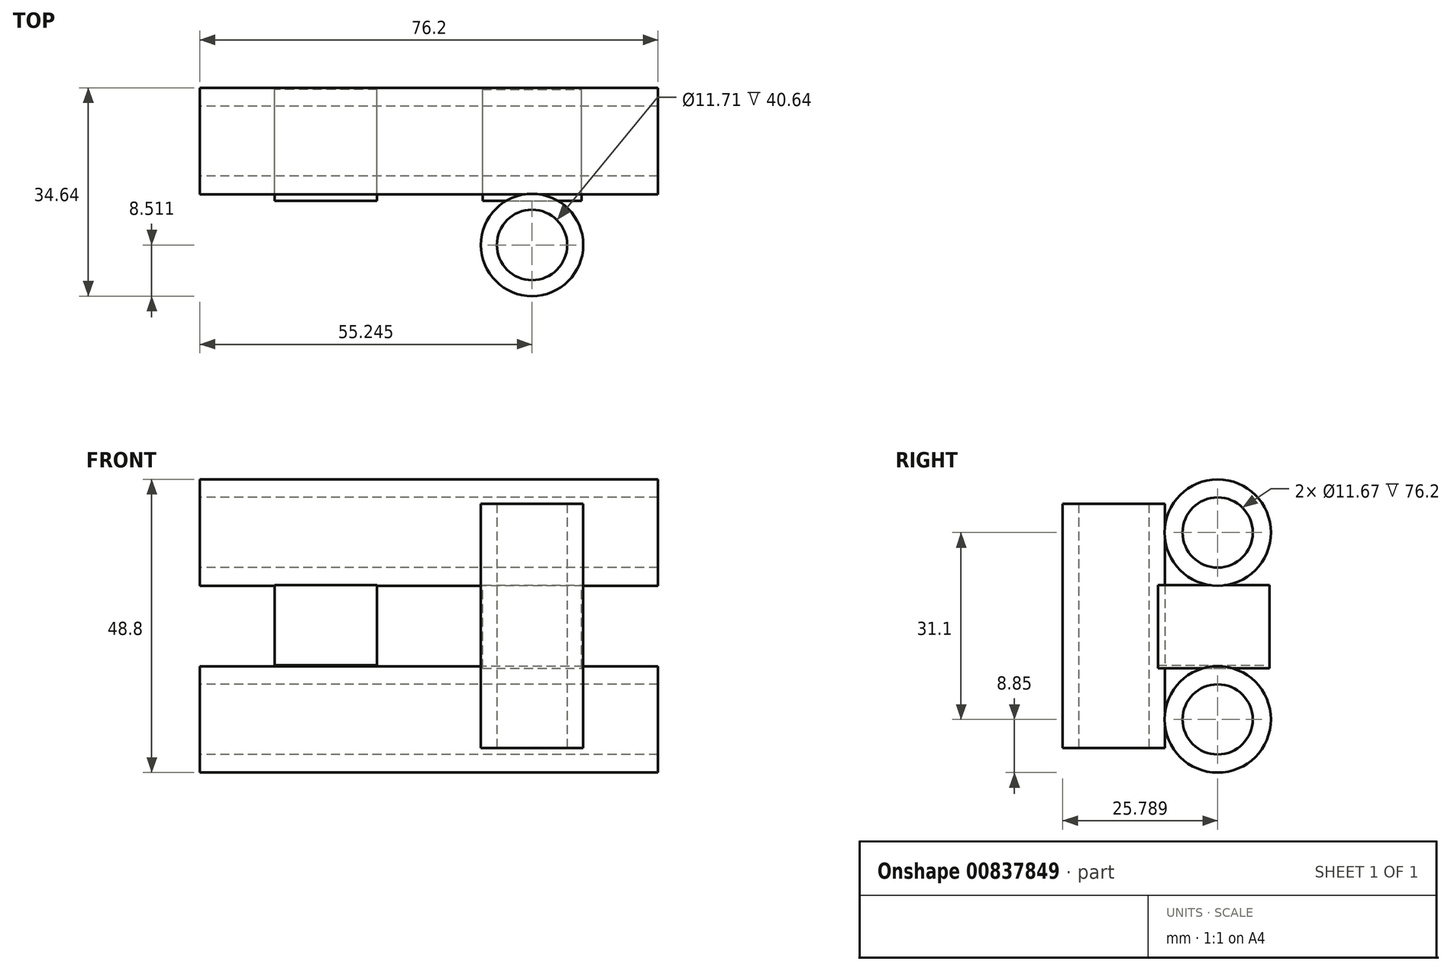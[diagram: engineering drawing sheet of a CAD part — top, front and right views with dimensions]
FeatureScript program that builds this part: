
annotation { "Feature Type Name" : "Feature", "Feature Type Description" : "" }
export const myFeature = defineFeature(function(context is Context, id is Id, definition is map)
    precondition{}
    {
        {
            var Q0;
            Q0=qCreatedBy(makeId("Front.planeOp"),FACE);
            var sketch = newSketch(context, id + "F0", { "sketchPlane" : qUnion([Q0])});
            skCircle(sketch, "E0", {"center": v(0, 0) * mm, "radius": 7.62 * mm});
            skCircle(sketch, "E1", {"center": v(0, 0) * mm, "radius": 8.9 * mm});
            skSolve(sketch);
        }
        {
            var Q0;
            Q0=sQuery(id+"F0.wireOp",EDGE,"E1");
            var Q1;
            Q1=sQuery(id+"F0.wireOp",EDGE,"E0");
            extrude(context, id + "F1", {"bodyType" : ToolBodyType.SURFACE, "surfaceEntities" : qUnion([Q0, Q1]), "depth" : 50.8 * mm, "offsetDistance" : 25.4 * mm, "hasSecondDirection" : true, "secondDirectionOppositeDirection" : true, "secondDirectionDepth" : 0.76 * mm});
        }
        {
            var Q0;
            Q0=qCreatedBy(makeId("Right.planeOp"),FACE);
            var sketch = newSketch(context, id + "F2", { "sketchPlane" : qUnion([Q0])});
            skLineSegment(sketch, "E2", {"start": v(-7.84, 9.17) * mm, "end": v(-7.84, 9.71) * mm});
            skCircle(sketch, "E3", {"center": v(-7.84, 15.55) * mm, "radius": 5.84 * mm});
            skCircle(sketch, "E4", {"center": v(-7.84, 15.55) * mm, "radius": 8.85 * mm});
            skCircle(sketch, "E5.MirrorC", {"center": v(-7.84, -15.55) * mm, "radius": 8.85 * mm});
            skCircle(sketch, "E6.MirrorC", {"center": v(-7.84, -15.55) * mm, "radius": 5.84 * mm});
            skLineSegment(sketch, "E7.trimOffspring", {"start": v(-7.84, 21.39) * mm, "end": v(-7.84, 21.93) * mm});
            skSolve(sketch);
        }
        {
            var Q0;
            Q0=qSketchRegion(id+"F2",true);
            extrude(context, id + "F3", {"entities" : qUnion([Q0]), "depth" : 38.1 * mm, "offsetDistance" : 25.4 * mm, "hasSecondDirection" : true, "secondDirectionOppositeDirection" : true, "secondDirectionDepth" : 38.1 * mm});
        }
        {
            var Q0;
            Q0=qCreatedBy(makeId("Top.planeOp"),FACE);
            var sketch = newSketch(context, id + "F4", { "sketchPlane" : qUnion([Q0])});
            skLineSegment(sketch, "E8", {"start": v(14.22, -16.88) * mm, "end": v(14.22, -17.13) * mm});
            skCircle(sketch, "E9", {"center": v(17.15, -25.12) * mm, "radius": 8.51 * mm});
            skPoint(sketch, "E10.orphan", {"position": v(0, -28.84) * mm});
            skCircle(sketch, "E11", {"center": v(17.15, -25.12) * mm, "radius": 5.85 * mm});
            skCircle(sketch, "E12.MirrorC", {"center": v(-17.15, -25.12) * mm, "radius": 8.51 * mm});
            skCircle(sketch, "E13.MirrorC", {"center": v(-17.15, -25.12) * mm, "radius": 5.85 * mm});
            skSolve(sketch);
        }
        {
            var Q0;
            Q0=makeQuery(id+"F4.imprint","IMPRINT",FACE,{"disambiguationData":[TD([[makeQuery(id+"F4.imprint","IMPRINT",EDGE,{"derivedFrom":sQuery(id+"F4.wireOp",EDGE,"E12.MirrorC")}),-1.0]])]});
            var Q1;
            Q1=makeQuery(id+"F4.imprint","IMPRINT",FACE,{"disambiguationData":[TD([[makeQuery(id+"F4.imprint","IMPRINT",EDGE,{"derivedFrom":sQuery(id+"F4.wireOp",EDGE,"E11")}),-1.0]])]});
            extrude(context, id + "F5", {"entities" : qUnion([Q0, Q1]), "depth" : 20.32 * mm, "offsetDistance" : 25.4 * mm, "hasSecondDirection" : true, "secondDirectionOppositeDirection" : true, "secondDirectionDepth" : 20.32 * mm});
        }
        {
            var Q0;
            Q0=qCreatedBy(makeId("Front.planeOp"),FACE);
            var sketch = newSketch(context, id + "F6", { "sketchPlane" : qUnion([Q0])});
            skLineSegment(sketch, "E14.bottom", {"start": v(8.9, -7.04) * mm, "end": v(25.39, -7.04) * mm});
            skLineSegment(sketch, "E14.top", {"start": v(8.9, 6.78) * mm, "end": v(25.39, 6.78) * mm});
            skLineSegment(sketch, "E14.left", {"start": v(8.9, -7.04) * mm, "end": v(8.9, 6.78) * mm});
            skLineSegment(sketch, "E14.right", {"start": v(25.39, -7.04) * mm, "end": v(25.39, 6.78) * mm});
            skLineSegment(sketch, "E15.bottom", {"start": v(-8.64, -6.51) * mm, "end": v(-25.65, -6.51) * mm});
            skLineSegment(sketch, "E15.top", {"start": v(-8.64, 6.78) * mm, "end": v(-25.65, 6.78) * mm});
            skLineSegment(sketch, "E15.left", {"start": v(-8.64, -6.51) * mm, "end": v(-8.64, 6.78) * mm});
            skLineSegment(sketch, "E15.right", {"start": v(-25.65, -6.51) * mm, "end": v(-25.65, 6.78) * mm});
            skSolve(sketch);
        }
        {
            var Q0;
            Q0=qSketchRegion(id+"F6",true);
            extrude(context, id + "F7", {"entities" : qUnion([Q0]), "depth" : 17.78 * mm, "offsetDistance" : 25.4 * mm, "hasSecondDirection" : true, "secondDirectionOppositeDirection" : true, "secondDirectionDepth" : 0.76 * mm});
        }
    });
